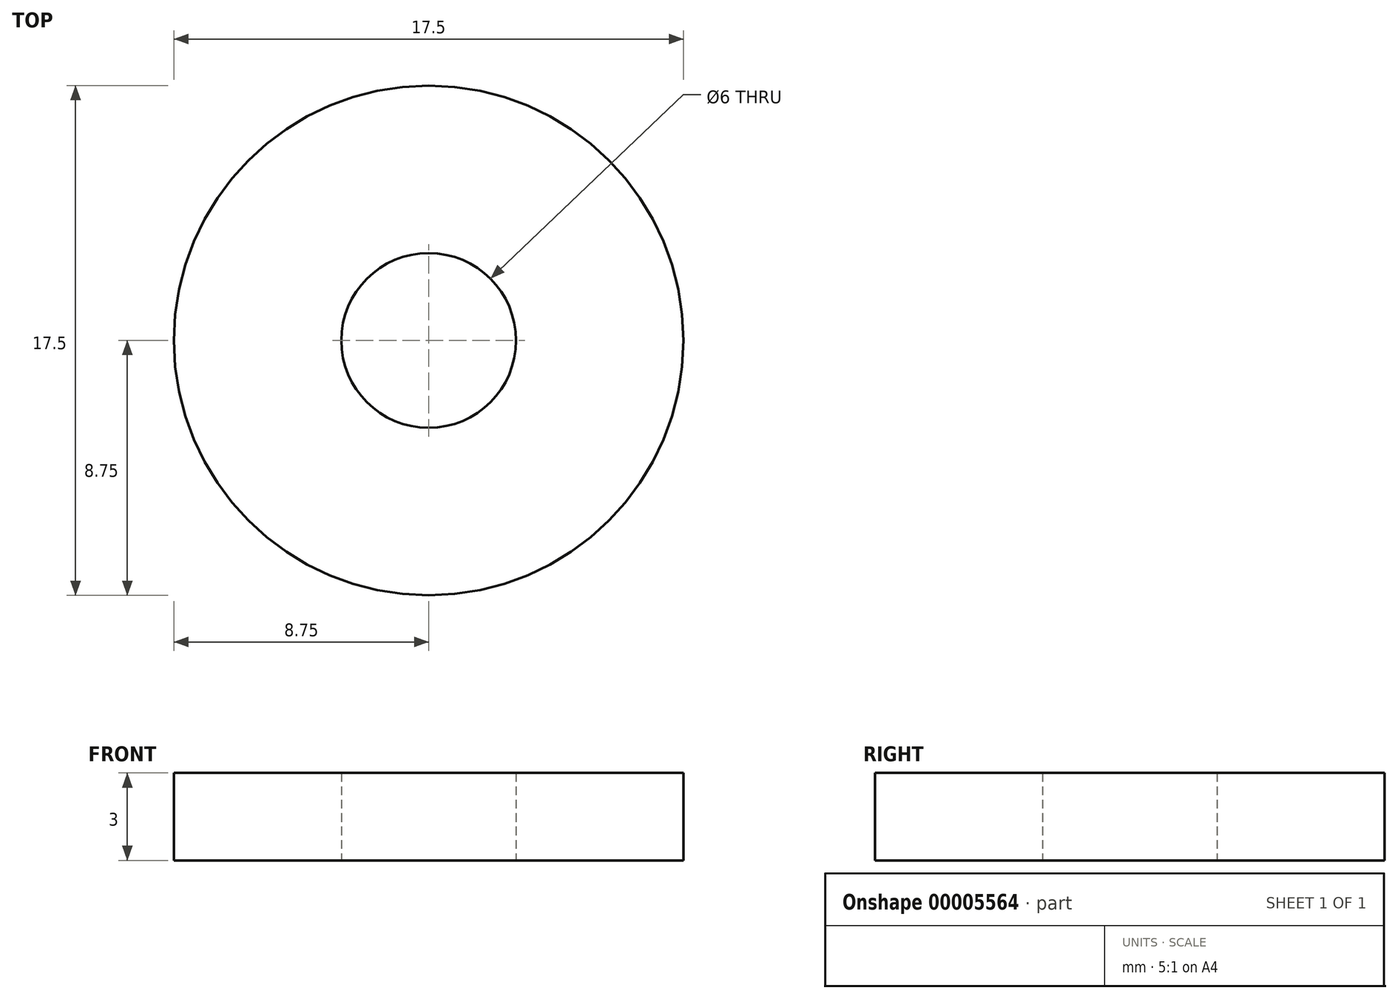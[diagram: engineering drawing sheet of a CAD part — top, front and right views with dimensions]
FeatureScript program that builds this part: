
annotation { "Feature Type Name" : "Feature", "Feature Type Description" : "" }
export const myFeature = defineFeature(function(context is Context, id is Id, definition is map)
    precondition{}
    {
        {
            var Q0;
            Q0=qCreatedBy(makeId("Top.planeOp"),FACE);
            var sketch = newSketch(context, id + "F0", { "sketchPlane" : qUnion([Q0])});
            skCircle(sketch, "E0", {"center": v(0, 0) * mm, "radius": 8.75 * mm});
            skCircle(sketch, "E1", {"center": v(0, 0) * mm, "radius": 3 * mm});
            skSolve(sketch);
        }
        {
            var Q0;
            Q0=makeQuery(id+"F0.imprint","IMPRINT",FACE,{"disambiguationData":[TD([[makeQuery(id+"F0.imprint","IMPRINT",EDGE,{"derivedFrom":sQuery(id+"F0.wireOp",EDGE,"E0")}),1.0]])]});
            extrude(context, id + "F1", {"entities" : qUnion([Q0]), "depth" : 3 * mm});
        }
    });
